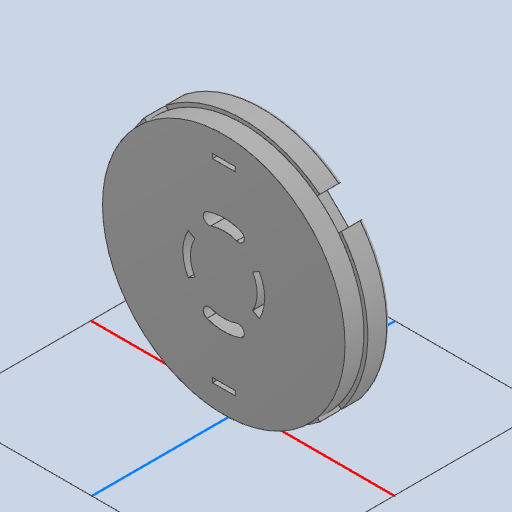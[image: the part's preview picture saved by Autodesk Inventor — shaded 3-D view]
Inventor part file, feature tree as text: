
AUTODESK INVENTOR PART (.ipt)
format: ipt  version: 2022 (Build 260153000, 153)  size: 199,168 bytes
history: native  units: mm
features: other x1, fillet x1
ambient origin geometry x8: Origin, YZ Plane, XZ Plane, XY Plane, X Axis, Y Axis, Z Axis, Center Point
bodies: Body1 (feature_tree)
feature tree (2):
  other  "Твердое тело1"
  fillet  "Fillet2"  [1 undecoded]
note: 1 required parameter value undecoded (feature->parameter linkage not recoverable at this tier; creation-order binding heuristic only, values carry confidence <= 0.55)
